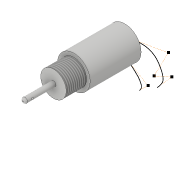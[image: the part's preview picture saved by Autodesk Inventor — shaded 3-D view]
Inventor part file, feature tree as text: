
AUTODESK INVENTOR PART (.ipt)
format: ipt  version: 2019 (Build 230136000, 136)  size: 120,320 bytes
history: native  units: in
note: dims shown in document units (in); Inventor stores cm internally (conversion verified against a paired STEP export)
features: sketch x7, extrude x6, thread x1, fillet x1
ambient origin geometry x8: Origin, YZ Plane, XZ Plane, XY Plane, X Axis, Y Axis, Z Axis, Center Point
bodies: Solid1 (feature_tree)
feature tree (15):
  extrude  "Extrusion1"  Depth=1.9685in TaperAngle=0.0deg
  extrude  "Extrusion2"  Depth=0.7874in TaperAngle=0.0deg
  thread  "Thread1"  [1 undecoded]
  extrude  "Extrusion3"  Depth=1.1811in TaperAngle=0.0deg
  extrude  "Extrusion4"  Depth=0.0787in
  fillet  "Fillet1"  [1 undecoded]
  extrude  "Extrusion5"  Depth=0.0394in
  extrude  "Extrusion6"  Depth=0.0669in TaperAngle=0.0deg
  sketch  "Sketch7"  dims[d20=0.0394in d21=0.0669in d22=0.0in]
  sketch  "Sketch1"  dims[d0=1.2598in d1=1.9685in d2=0.0in]
  sketch  "Sketch2"  dims[d3=0.9843in d4=0.7874in d5=0.0in d6=0.3937in d7=0.0in]
  sketch  "Sketch3"  dims[d8=0.1969in d9=1.1811in d10=0.0in]
  sketch  "Sketch4"  dims[d11=0.2756in d12=0.0787in d13=0.0in d14=0.0in]
  sketch  "Sketch5"  dims[d15=0.0787in d16=0.0394in]
  sketch  "Sketch6"  dims[d17=0.0394in d18=0.0669in d19=0.0in]
note: 2 required parameter values undecoded (feature->parameter linkage not recoverable at this tier; creation-order binding heuristic only, values carry confidence <= 0.55)
